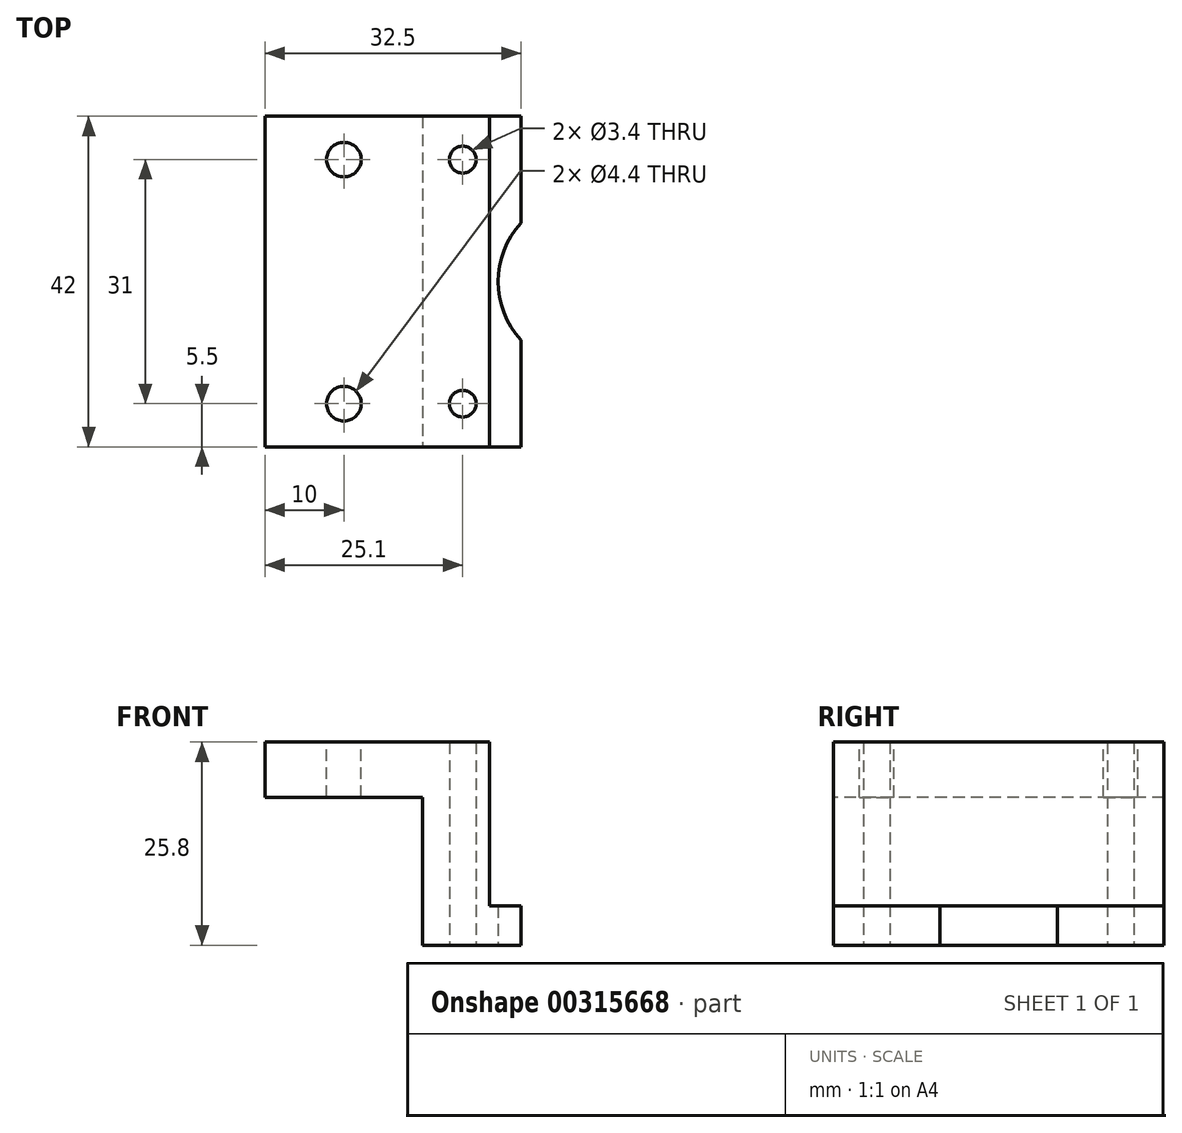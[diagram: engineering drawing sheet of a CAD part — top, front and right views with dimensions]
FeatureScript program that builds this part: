
annotation { "Feature Type Name" : "Feature", "Feature Type Description" : "" }
export const myFeature = defineFeature(function(context is Context, id is Id, definition is map)
    precondition{}
    {
        {
            var Q0;
            Q0=qCreatedBy(makeId("Front.planeOp"),FACE);
            var sketch = newSketch(context, id + "F0", { "sketchPlane" : qUnion([Q0])});
            skLineSegment(sketch, "E0", {"start": v(8.5, 25.8) * mm, "end": v(8.5, 5) * mm});
            skLineSegment(sketch, "E1", {"start": v(8.5, 5) * mm, "end": v(12.5, 5) * mm});
            skLineSegment(sketch, "E2", {"start": v(12.5, 5) * mm, "end": v(12.5, 0) * mm});
            skLineSegment(sketch, "E3", {"start": v(12.5, 0) * mm, "end": v(0, 0) * mm});
            skLineSegment(sketch, "E4", {"start": v(0, 0) * mm, "end": v(0, 25.8) * mm});
            skLineSegment(sketch, "E5", {"start": v(0, 25.8) * mm, "end": v(8.5, 25.8) * mm});
            skSolve(sketch);
        }
        {
            var Q0;
            Q0=qSketchRegion(id+"F0",true);
            extrude(context, id + "F1", {"entities" : qUnion([Q0]), "oppositeDirection" : true, "depth" : 42 * mm});
        }
        {
            var Q0;
            Q0=makeQuery(id+"F1.opExtrude","SWEPT_FACE",FACE,{"disambiguationData":[OSD([sQuery(id+"F0.wireOp",EDGE,"E3")])]});
            var sketch = newSketch(context, id + "F2", { "sketchPlane" : qUnion([Q0])});
            skCircle(sketch, "E6", {"center": v(5.1, -5.5) * mm, "radius": 1.7 * mm});
            skCircle(sketch, "E7", {"center": v(5.1, -36.5) * mm, "radius": 1.7 * mm});
            skCircle(sketch, "E8", {"center": v(20.6, -21) * mm, "radius": 11 * mm});
            skLineSegment(sketch, "E9", {"start": v(0, -21) * mm, "end": v(12.5, -21) * mm, "construction": true});
            skSolve(sketch);
        }
        {
            var Q0;
            Q0=qSketchRegion(id+"F2",true);
            extrude(context, id + "F3", {"entities" : qUnion([Q0]), "operationType" : NewBodyOperationType.REMOVE, "endBound" : BoundingType.THROUGH_ALL, "oppositeDirection" : true, "depth" : 25 * mm});
        }
        {
            var Q0;
            Q0=makeQuery(id+"F1.opExtrude","SWEPT_FACE",FACE,{"disambiguationData":[OSD([sQuery(id+"F0.wireOp",EDGE,"E4")])]});
            var sketch = newSketch(context, id + "F4", { "sketchPlane" : qUnion([Q0])});
            skLineSegment(sketch, "E10.bottom", {"start": v(-42, 25.8) * mm, "end": v(0, 25.8) * mm});
            skLineSegment(sketch, "E10.top", {"start": v(-42, 18.8) * mm, "end": v(0, 18.8) * mm});
            skLineSegment(sketch, "E10.left", {"start": v(-42, 25.8) * mm, "end": v(-42, 18.8) * mm});
            skLineSegment(sketch, "E10.right", {"start": v(0, 25.8) * mm, "end": v(0, 18.8) * mm});
            skSolve(sketch);
        }
        {
            var Q0;
            Q0=qSketchRegion(id+"F4",true);
            extrude(context, id + "F5", {"entities" : qUnion([Q0]), "operationType" : NewBodyOperationType.ADD, "depth" : 20 * mm});
        }
        {
            var Q0;
            Q0=makeQuery(id+"F5.boolean.opBoolean","MERGE",FACE,{"derivedFrom":[makeQuery(id+"F1.opExtrude","SWEPT_FACE",FACE,{"disambiguationData":[OSD([sQuery(id+"F0.wireOp",EDGE,"E5")])]}),makeQuery(id+"F5.opExtrude","SWEPT_FACE",FACE,{"disambiguationData":[OSD([sQuery(id+"F4.wireOp",EDGE,"E10.bottom")])]})]});
            var sketch = newSketch(context, id + "F6", { "sketchPlane" : qUnion([Q0])});
            skCircle(sketch, "E11", {"center": v(-10, 36.5) * mm, "radius": 2.2 * mm});
            skCircle(sketch, "E12", {"center": v(-10, 5.5) * mm, "radius": 2.2 * mm});
            skPoint(sketch, "E13", {"position": v(5.1, 36.5) * mm});
            skPoint(sketch, "E14", {"position": v(5.1, 5.5) * mm});
            skSolve(sketch);
        }
        {
            var Q0;
            Q0=qSketchRegion(id+"F6",true);
            extrude(context, id + "F7", {"entities" : qUnion([Q0]), "operationType" : NewBodyOperationType.REMOVE, "oppositeDirection" : true, "depth" : 25 * mm});
        }
        {
            var Q0;
            Q0=makeQuery(id+"F5.boolean.opBoolean","MERGE",FACE,{"derivedFrom":[makeQuery(id+"F1.opExtrude","SWEPT_FACE",FACE,{"disambiguationData":[OSD([sQuery(id+"F0.wireOp",EDGE,"E5")])]}),makeQuery(id+"F5.opExtrude","SWEPT_FACE",FACE,{"disambiguationData":[OSD([sQuery(id+"F4.wireOp",EDGE,"E10.bottom")])]})]});
            var sketch = newSketch(context, id + "F8", { "sketchPlane" : qUnion([Q0])});
            skText(sketch, "E15", { "text": "R", "fontName": "OpenSans-Bold.ttf"});
            const initialGuessF8  = {"E15": [-0.02, 0.03407, 0, -1, 0.0285]};
            skSetInitialGuess(sketch, initialGuessF8);
            skSolve(sketch);
        }
        {
            var Q0;
            Q0=qSketchRegion(id+"F8",true);
            extrude(context, id + "F9", {"entities" : qUnion([Q0]), "operationType" : NewBodyOperationType.ADD, "depth" : 1 * mm});
        }
        {
            var Q0;
            Q0=makeQuery(id+"F9.opExtrude","CAP_FACE",FACE,{"disambiguationData":[OSD([sQuery(id+"F8.wireOp",EDGE,"E15.sketch_text.stroke-0"),sQuery(id+"F8.wireOp",EDGE,"E15.sketch_text.stroke-1"),sQuery(id+"F8.wireOp",EDGE,"E15.sketch_text.stroke-2"),sQuery(id+"F8.wireOp",EDGE,"E15.sketch_text.stroke-3"),sQuery(id+"F8.wireOp",EDGE,"E15.sketch_text.stroke-4"),sQuery(id+"F8.wireOp",EDGE,"E15.sketch_text.stroke-5"),sQuery(id+"F8.wireOp",EDGE,"E15.sketch_text.stroke-6"),sQuery(id+"F8.wireOp",EDGE,"E15.sketch_text.stroke-7"),sQuery(id+"F8.wireOp",EDGE,"E15.sketch_text.stroke-8"),sQuery(id+"F8.wireOp",EDGE,"E15.sketch_text.stroke-9"),sQuery(id+"F8.wireOp",EDGE,"E15.sketch_text.stroke-10"),sQuery(id+"F8.wireOp",EDGE,"E15.sketch_text.stroke-11"),sQuery(id+"F8.wireOp",EDGE,"E15.sketch_text.stroke-12"),sQuery(id+"F8.wireOp",EDGE,"E15.sketch_text.stroke-13"),sQuery(id+"F8.wireOp",EDGE,"E15.sketch_text.stroke-14"),sQuery(id+"F8.wireOp",EDGE,"E15.sketch_text.stroke-15"),sQuery(id+"F8.wireOp",EDGE,"E15.sketch_text.stroke-16"),sQuery(id+"F8.wireOp",EDGE,"E15.sketch_text.stroke-17"),sQuery(id+"F8.wireOp",EDGE,"E15.sketch_text.stroke-18")])],"isStart":false});
            extrude(context, id + "F10", {"entities" : qUnion([Q0]), "operationType" : NewBodyOperationType.REMOVE, "oppositeDirection" : true, "depth" : 1 * mm});
        }
    });
